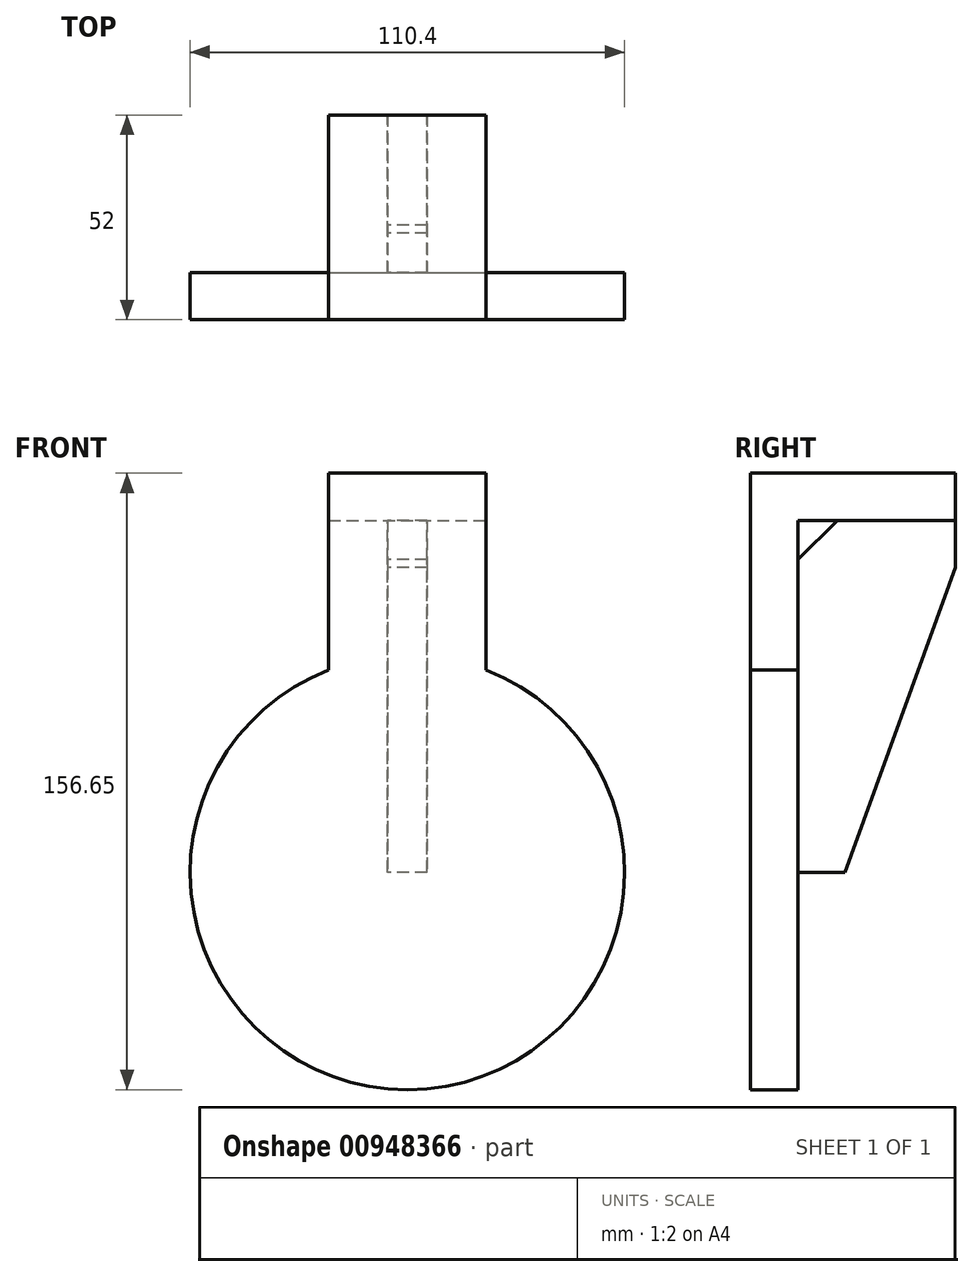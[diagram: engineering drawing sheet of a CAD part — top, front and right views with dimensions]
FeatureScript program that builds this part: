
annotation { "Feature Type Name" : "Feature", "Feature Type Description" : "" }
export const myFeature = defineFeature(function(context is Context, id is Id, definition is map)
    precondition{}
    {
        {
            var Q0;
            Q0=qCreatedBy(makeId("Front.planeOp"),FACE);
            var sketch = newSketch(context, id + "F0", { "sketchPlane" : qUnion([Q0])});
            skCircle(sketch, "E0", {"center": v(0, 0) * mm, "radius": 55.2 * mm});
            skLineSegment(sketch, "E1.bottom", {"start": v(-20, 51.45) * mm, "end": v(20, 51.45) * mm});
            skLineSegment(sketch, "E1.top", {"start": v(-20, 101.45) * mm, "end": v(20, 101.45) * mm});
            skLineSegment(sketch, "E1.left", {"start": v(-20, 51.45) * mm, "end": v(-20, 101.45) * mm});
            skLineSegment(sketch, "E1.right", {"start": v(20, 51.45) * mm, "end": v(20, 101.45) * mm});
            skSolve(sketch);
        }
        {
            var Q0;
            Q0 = qSketchRegion(id + "F0", true);
            extrude(context, id + "F1", {"entities" : qUnion([Q0]), "endBound" : BoundingType.SYMMETRIC, "depth" : 12 * mm, "offsetDistance" : 25 * mm});
        }
        {
            var Q0;
            Q0=makeQuery(id+"F1.opExtrude","SWEPT_FACE",FACE,{"disambiguationData":[OSD([sQuery(id+"F0.wireOp",EDGE,"E1.top")])]});
            var sketch = newSketch(context, id + "F2", { "sketchPlane" : qUnion([Q0])});
            skLineSegment(sketch, "E2.bottom", {"start": v(-20, 6) * mm, "end": v(20, 6) * mm});
            skLineSegment(sketch, "E2.top", {"start": v(-20, 46) * mm, "end": v(20, 46) * mm});
            skLineSegment(sketch, "E2.left", {"start": v(-20, 6) * mm, "end": v(-20, 46) * mm});
            skLineSegment(sketch, "E2.right", {"start": v(20, 6) * mm, "end": v(20, 46) * mm});
            skSolve(sketch);
        }
        {
            var Q0;
            Q0 = qSketchRegion(id + "F2", true);
            extrude(context, id + "F3", {"entities" : qUnion([Q0]), "operationType" : NewBodyOperationType.ADD, "oppositeDirection" : true, "depth" : 12 * mm, "offsetDistance" : 25 * mm});
        }
        {
            var Q0;
            Q0=qCreatedBy(makeId("Right.planeOp"),FACE);
            var sketch = newSketch(context, id + "F4", { "sketchPlane" : qUnion([Q0])});
            skLineSegment(sketch, "E3", {"start": v(46, 89.45) * mm, "end": v(46, 77.45) * mm});
            skLineSegment(sketch, "E4", {"start": v(46, 77.45) * mm, "end": v(18, 0) * mm});
            skLineSegment(sketch, "E5", {"start": v(18, 0) * mm, "end": v(6, 0) * mm});
            skLineSegment(sketch, "E6", {"start": v(6, 0) * mm, "end": v(6, 79.45) * mm});
            skLineSegment(sketch, "E7", {"start": v(6, 79.45) * mm, "end": v(16, 89.45) * mm});
            skLineSegment(sketch, "E8", {"start": v(16, 89.45) * mm, "end": v(46, 89.45) * mm});
            skSolve(sketch);
        }
        {
            var Q0;
            Q0 = qSketchRegion(id + "F4", true);
            extrude(context, id + "F5", {"entities" : qUnion([Q0]), "endBound" : BoundingType.SYMMETRIC, "depth" : 10 * mm, "offsetDistance" : 25 * mm});
        }
    });
